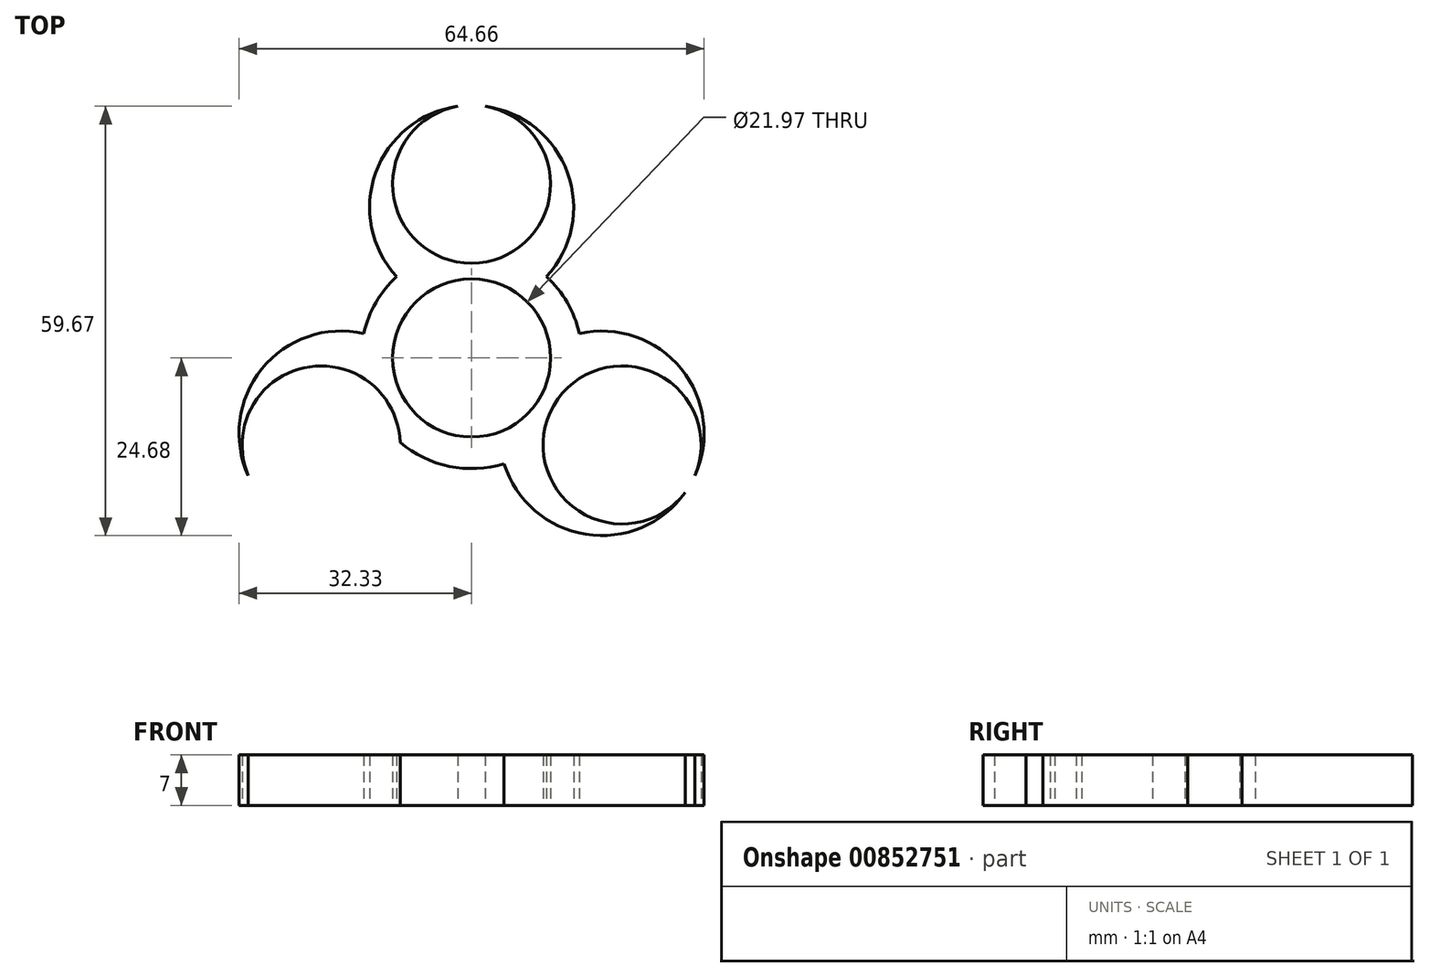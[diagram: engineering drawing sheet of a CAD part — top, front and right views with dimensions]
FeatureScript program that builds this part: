
annotation { "Feature Type Name" : "Feature", "Feature Type Description" : "" }
export const myFeature = defineFeature(function(context is Context, id is Id, definition is map)
    precondition{}
    {
        {
            var Q0;
            Q0=qCreatedBy(makeId("Top.planeOp"),FACE);
            var sketch = newSketch(context, id + "F0", { "sketchPlane" : qUnion([Q0])});
            skCircle(sketch, "E0.cCircle", {"center": v(0, 0) * mm, "radius": 20.93 * mm, "construction": true});
            skLineSegment(sketch, "E0.0", {"start": v(20.93, 12.08) * mm, "end": v(20.93, -12.08) * mm, "construction": true});
            skLineSegment(sketch, "E0.1", {"start": v(20.93, -12.08) * mm, "end": v(0, -24.17) * mm, "construction": true});
            skLineSegment(sketch, "E0.2", {"start": v(0, -24.17) * mm, "end": v(-20.93, -12.08) * mm, "construction": true});
            skLineSegment(sketch, "E0.3", {"start": v(-20.93, -12.08) * mm, "end": v(-20.93, 12.08) * mm, "construction": true});
            skLineSegment(sketch, "E0.4", {"start": v(-20.93, 12.08) * mm, "end": v(0, 24.17) * mm, "construction": true});
            skLineSegment(sketch, "E0.5", {"start": v(0, 24.17) * mm, "end": v(20.93, 12.08) * mm, "construction": true});
            skPoint(sketch, "E0.0.midPoint", {"position": v(20.93, 0) * mm});
            skCircle(sketch, "E1", {"center": v(0, 0) * mm, "radius": 10.99 * mm});
            skLineSegment(sketch, "E2", {"start": v(0, 0) * mm, "end": v(0, 24.17) * mm, "construction": true});
            skLineSegment(sketch, "E3", {"start": v(0, 0) * mm, "end": v(20.93, -12.08) * mm, "construction": true});
            skLineSegment(sketch, "E4", {"start": v(0, 0) * mm, "end": v(-20.93, -12.08) * mm, "construction": true});
            skCircle(sketch, "E5.cCircle", {"center": v(-20.93, -12.08) * mm, "radius": 6.6 * mm, "construction": true});
            skLineSegment(sketch, "E5.0", {"start": v(-20.93, 1.11) * mm, "end": v(-9.5, -18.68) * mm, "construction": true});
            skLineSegment(sketch, "E5.1", {"start": v(-9.5, -18.68) * mm, "end": v(-32.36, -18.68) * mm, "construction": true});
            skLineSegment(sketch, "E5.2", {"start": v(-32.36, -18.68) * mm, "end": v(-20.93, 1.11) * mm, "construction": true});
            skPoint(sketch, "E5.0.midPoint", {"position": v(-15.21, -8.78) * mm});
            skCircle(sketch, "E6.cCircle", {"center": v(0, 24.17) * mm, "radius": 6.6 * mm, "construction": true});
            skLineSegment(sketch, "E6.0", {"start": v(11.43, 17.57) * mm, "end": v(-11.43, 17.57) * mm, "construction": true});
            skLineSegment(sketch, "E6.1", {"start": v(-11.43, 17.57) * mm, "end": v(0, 37.37) * mm, "construction": true});
            skLineSegment(sketch, "E6.2", {"start": v(0, 37.37) * mm, "end": v(11.43, 17.57) * mm, "construction": true});
            skPoint(sketch, "E6.0.midPoint", {"position": v(0, 17.57) * mm});
            skCircle(sketch, "E7.cCircle", {"center": v(20.93, -12.08) * mm, "radius": 6.6 * mm, "construction": true});
            skLineSegment(sketch, "E7.0", {"start": v(9.5, -18.68) * mm, "end": v(20.93, 1.11) * mm, "construction": true});
            skLineSegment(sketch, "E7.1", {"start": v(20.93, 1.11) * mm, "end": v(32.36, -18.68) * mm, "construction": true});
            skLineSegment(sketch, "E7.2", {"start": v(32.36, -18.68) * mm, "end": v(9.5, -18.68) * mm, "construction": true});
            skPoint(sketch, "E7.0.midPoint", {"position": v(15.21, -8.78) * mm});
            skArc(sketch, "E8", {"start": v(-30.58, -17.33) * mm, "mid": v(-30.17, -18.02) * mm, "end": v(-29.71, -18.68) * mm});
            skArc(sketch, "E9", {"start": v(-29.71, -18.68) * mm, "mid": v(-11.69, -6.14) * mm, "end": v(-30.58, -17.33) * mm});
            skArc(sketch, "E10", {"start": v(30.97, -16.54) * mm, "mid": v(11.42, -6.6) * mm, "end": v(29.81, -18.55) * mm});
            skArc(sketch, "E11", {"start": v(29.81, -18.55) * mm, "mid": v(30.44, -17.58) * mm, "end": v(30.97, -16.54) * mm});
            skArc(sketch, "E12", {"start": v(1.9, 34.99) * mm, "mid": v(0.3, 35.15) * mm, "end": v(-1.33, 35.07) * mm});
            skArc(sketch, "E13", {"start": v(-1.33, 35.07) * mm, "mid": v(-0.3, 13.19) * mm, "end": v(1.9, 34.99) * mm});
            skArc(sketch, "E14", {"start": v(-1.31, 35.05) * mm, "mid": v(-0.3, 6.75) * mm, "end": v(1.9, 34.99) * mm});
            skArc(sketch, "E15", {"start": v(-29.71, -18.68) * mm, "mid": v(-5.8, -3.36) * mm, "end": v(-31.04, -16.37) * mm});
            skArc(sketch, "E16", {"start": v(31.03, -16.4) * mm, "mid": v(5.8, -3.35) * mm, "end": v(29.71, -18.68) * mm});
            skPoint(sketch, "E17", {"position": v(-31.04, -16.37) * mm});
            skCircle(sketch, "E18", {"center": v(0, 0) * mm, "radius": 15.37 * mm});
            skSolve(sketch);
        }
        {
            var Q0;
            {var subQ0=sQuery(id+"F0.wireOp",EDGE,"E14");var subQ1=sQuery(id+"F0.wireOp",EDGE,"E13");var subQ2=makeQuery(id+"F0.imprint","INTERSECT",VERTEX,{"derivedFrom":[subQ1,subQ0]});Q0=makeQuery(id+"F0.imprint","IMPRINT",FACE,{"disambiguationData":[TD([[makeQuery(id+"F0.imprint","IMPRINT",EDGE,{"disambiguationData":[TD([[subQ2,-1.0]])],"derivedFrom":subQ1}),-1.0]])]});}
            var Q1;
            {var subQ0=sQuery(id+"F0.wireOp",EDGE,"E14");var subQ3=sQuery(id+"F0.wireOp",EDGE,"E18");var subQ5=makeQuery(id+"F0.imprint","INTERSECT",VERTEX,{"disambiguationData":[OD(1.0)],"derivedFrom":[subQ0,subQ3]});Q1=makeQuery(id+"F0.imprint","IMPRINT",FACE,{"disambiguationData":[TD([[makeQuery(id+"F0.imprint","IMPRINT",EDGE,{"disambiguationData":[TD([[subQ5,-1.0]])],"derivedFrom":subQ3}),-1.0]])]});}
            var Q2;
            {var subQ0=sQuery(id+"F0.wireOp",EDGE,"E16");var subQ1=sQuery(id+"F0.wireOp",EDGE,"E10");var subQ2=makeQuery(id+"F0.imprint","INTERSECT",VERTEX,{"disambiguationData":[OD(1.0)],"derivedFrom":[subQ1,subQ0]});Q2=makeQuery(id+"F0.imprint","IMPRINT",FACE,{"disambiguationData":[TD([[makeQuery(id+"F0.imprint","IMPRINT",EDGE,{"disambiguationData":[TD([[subQ2,-1.0]])],"derivedFrom":subQ1}),-1.0]])]});}
            var Q3;
            {var subQ0=sQuery(id+"F0.wireOp",EDGE,"E16");var subQ1=sQuery(id+"F0.wireOp",EDGE,"E10");var subQ2=makeQuery(id+"F0.imprint","INTERSECT",VERTEX,{"disambiguationData":[OD(0.0)],"derivedFrom":[subQ1,subQ0]});Q3=makeQuery(id+"F0.imprint","IMPRINT",FACE,{"disambiguationData":[TD([[makeQuery(id+"F0.imprint","IMPRINT",EDGE,{"disambiguationData":[TD([[subQ2,1.0]])],"derivedFrom":subQ1}),-1.0]])]});}
            var Q4;
            {var subQ0=sQuery(id+"F0.wireOp",EDGE,"E15");var subQ3=sQuery(id+"F0.wireOp",EDGE,"E18");var subQ5=makeQuery(id+"F0.imprint","INTERSECT",VERTEX,{"disambiguationData":[OD(0.0)],"derivedFrom":[subQ0,subQ3]});Q4=makeQuery(id+"F0.imprint","IMPRINT",FACE,{"disambiguationData":[TD([[makeQuery(id+"F0.imprint","IMPRINT",EDGE,{"disambiguationData":[TD([[subQ5,1.0]])],"derivedFrom":subQ3}),-1.0]])]});}
            var Q5;
            {var subQ0=sQuery(id+"F0.wireOp",EDGE,"E15");var subQ1=sQuery(id+"F0.wireOp",EDGE,"E9");var subQ2=makeQuery(id+"F0.imprint","INTERSECT",VERTEX,{"derivedFrom":[subQ1,subQ0]});Q5=makeQuery(id+"F0.imprint","IMPRINT",FACE,{"disambiguationData":[TD([[makeQuery(id+"F0.imprint","IMPRINT",EDGE,{"disambiguationData":[TD([[subQ2,1.0]])],"derivedFrom":subQ1}),-1.0]])]});}
            var Q6;
            {var subQ0=sQuery(id+"F0.wireOp",EDGE,"E14");var subQ1=sQuery(id+"F0.wireOp",EDGE,"E1");var subQ2=makeQuery(id+"F0.imprint","INTERSECT",VERTEX,{"disambiguationData":[OD(1.0)],"derivedFrom":[subQ1,subQ0]});Q6=makeQuery(id+"F0.imprint","IMPRINT",FACE,{"disambiguationData":[TD([[makeQuery(id+"F0.imprint","IMPRINT",EDGE,{"disambiguationData":[TD([[subQ2,-1.0]])],"derivedFrom":subQ1}),-1.0]])]});}
            var Q7;
            {var subQ0=sQuery(id+"F0.wireOp",EDGE,"E15");var subQ1=sQuery(id+"F0.wireOp",EDGE,"E1");var subQ2=makeQuery(id+"F0.imprint","INTERSECT",VERTEX,{"disambiguationData":[OD(1.0)],"derivedFrom":[subQ1,subQ0]});Q7=makeQuery(id+"F0.imprint","IMPRINT",FACE,{"disambiguationData":[TD([[makeQuery(id+"F0.imprint","IMPRINT",EDGE,{"disambiguationData":[TD([[subQ2,-1.0]])],"derivedFrom":subQ1}),-1.0]])]});}
            var Q8;
            {var subQ0=sQuery(id+"F0.wireOp",EDGE,"E14");var subQ1=sQuery(id+"F0.wireOp",EDGE,"E1");var subQ2=makeQuery(id+"F0.imprint","INTERSECT",VERTEX,{"disambiguationData":[OD(0.0)],"derivedFrom":[subQ1,subQ0]});Q8=makeQuery(id+"F0.imprint","IMPRINT",FACE,{"disambiguationData":[TD([[makeQuery(id+"F0.imprint","IMPRINT",EDGE,{"disambiguationData":[TD([[subQ2,1.0]])],"derivedFrom":subQ1}),-1.0]])]});}
            var Q9;
            {var subQ1=sQuery(id+"F0.wireOp",EDGE,"E15");var subQ3=sQuery(id+"F0.wireOp",EDGE,"E1");var subQ4=makeQuery(id+"F0.imprint","INTERSECT",VERTEX,{"disambiguationData":[OD(0.0)],"derivedFrom":[subQ3,subQ1]});Q9=makeQuery(id+"F0.imprint","IMPRINT",FACE,{"disambiguationData":[TD([[makeQuery(id+"F0.imprint","IMPRINT",EDGE,{"disambiguationData":[TD([[subQ4,-1.0]])],"derivedFrom":subQ3}),-1.0]])]});}
            var Q10;
            {var subQ1=sQuery(id+"F0.wireOp",EDGE,"E16");var subQ3=sQuery(id+"F0.wireOp",EDGE,"E1");var subQ4=makeQuery(id+"F0.imprint","INTERSECT",VERTEX,{"disambiguationData":[OD(0.0)],"derivedFrom":[subQ3,subQ1]});Q10=makeQuery(id+"F0.imprint","IMPRINT",FACE,{"disambiguationData":[TD([[makeQuery(id+"F0.imprint","IMPRINT",EDGE,{"disambiguationData":[TD([[subQ4,1.0]])],"derivedFrom":subQ3}),-1.0]])]});}
            var Q11;
            {var subQ1=sQuery(id+"F0.wireOp",EDGE,"E14");var subQ3=sQuery(id+"F0.wireOp",EDGE,"E1");var subQ5=makeQuery(id+"F0.imprint","INTERSECT",VERTEX,{"disambiguationData":[OD(0.0)],"derivedFrom":[subQ3,subQ1]});Q11=makeQuery(id+"F0.imprint","IMPRINT",FACE,{"disambiguationData":[TD([[makeQuery(id+"F0.imprint","IMPRINT",EDGE,{"disambiguationData":[TD([[subQ5,-1.0]])],"derivedFrom":subQ3}),-1.0]])]});}
            extrude(context, id + "F1", {"entities" : qUnion([Q0, Q1, Q2, Q3, Q4, Q5, Q6, Q7, Q8, Q9, Q10, Q11]), "depth" : 7 * mm, "offsetDistance" : 25.4 * mm});
        }
    });
